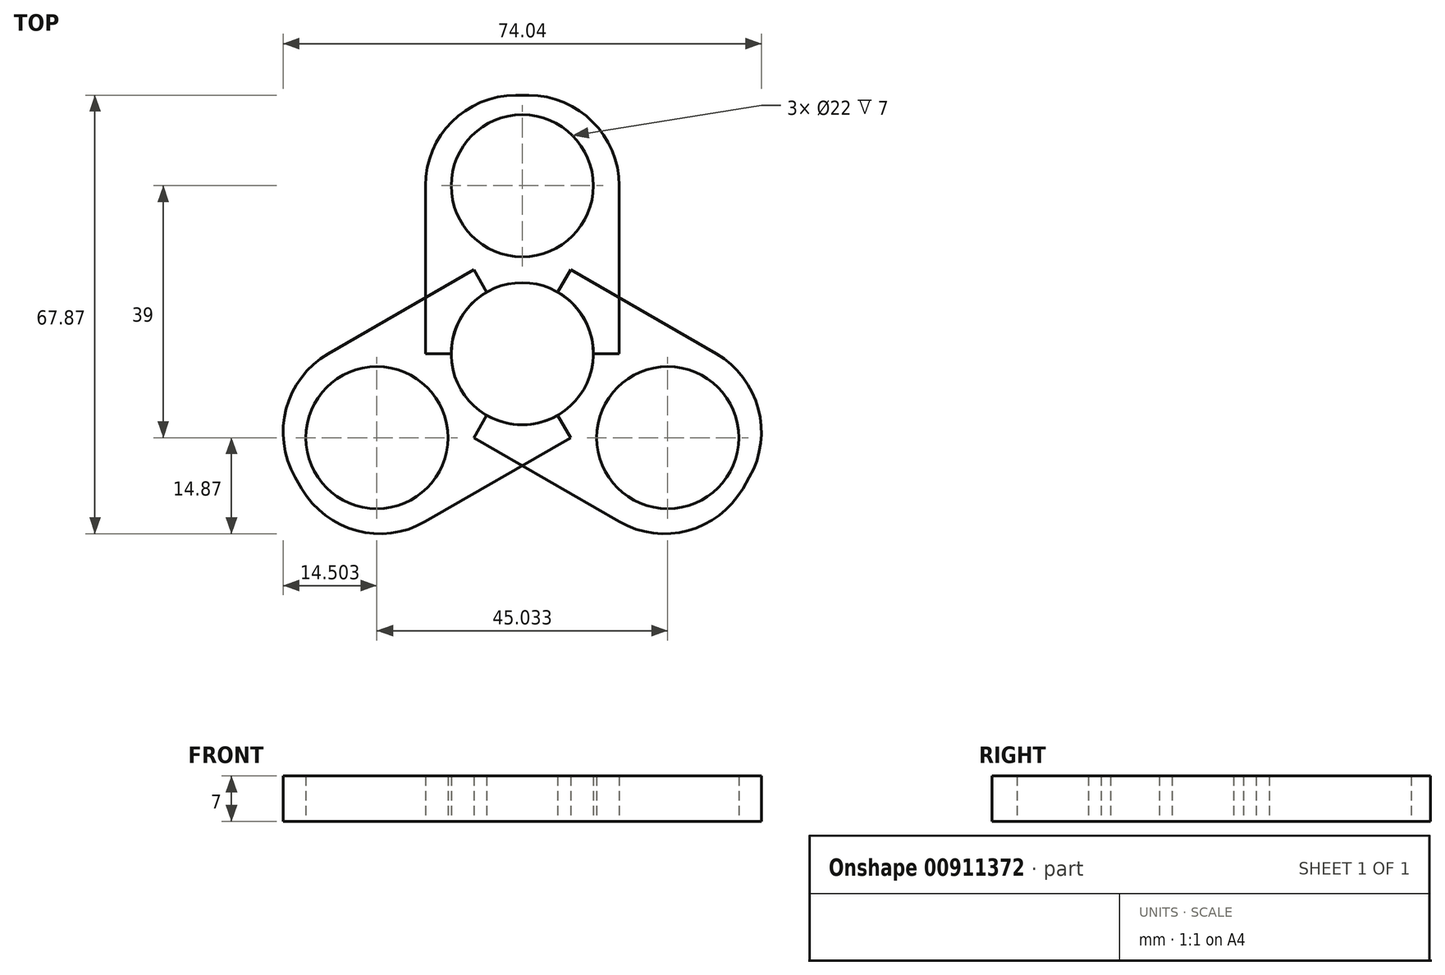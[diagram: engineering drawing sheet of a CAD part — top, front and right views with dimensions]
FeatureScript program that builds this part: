
annotation { "Feature Type Name" : "Feature", "Feature Type Description" : "" }
export const myFeature = defineFeature(function(context is Context, id is Id, definition is map)
    precondition{}
    {
        {
            var Q0;
            Q0=qCreatedBy(makeId("Top.planeOp"),FACE);
            var sketch = newSketch(context, id + "F0", { "sketchPlane" : qUnion([Q0])});
            skCircle(sketch, "E0", {"center": v(0, 0) * mm, "radius": 11 * mm});
            skLineSegment(sketch, "E1.bottom", {"start": v(0, 0) * mm, "end": v(15, 0) * mm});
            skLineSegment(sketch, "E1.top", {"start": v(0, 40) * mm, "end": v(1, 40) * mm});
            skLineSegment(sketch, "E1.left", {"start": v(0, 0) * mm, "end": v(0, 40) * mm});
            skLineSegment(sketch, "E1.right", {"start": v(15, 0) * mm, "end": v(15, 26) * mm});
            skLineSegment(sketch, "E2.bottom", {"start": v(0, 0) * mm, "end": v(-15, 0) * mm});
            skLineSegment(sketch, "E2.top", {"start": v(0, 40) * mm, "end": v(-1, 40) * mm});
            skLineSegment(sketch, "E2.right", {"start": v(-15, 0) * mm, "end": v(-15, 26) * mm});
            skLineSegment(sketch, "E3", {"start": v(0, 40) * mm, "end": v(0, 26) * mm});
            skCircle(sketch, "E4", {"center": v(0, 26) * mm, "radius": 11 * mm});
            skPoint(sketch, "E5.visualSharp", {"position": v(-15, 40) * mm});
            skArc(sketch, "E5.filletArc", {"start": v(-1, 40) * mm, "mid": v(-10.9, 35.9) * mm, "end": v(-15, 26) * mm});
            skPoint(sketch, "E6.visualSharp", {"position": v(15, 40) * mm});
            skArc(sketch, "E6.filletArc", {"start": v(15, 26) * mm, "mid": v(10.9, 35.9) * mm, "end": v(1, 40) * mm});
            skSolve(sketch);
        }
        {
            var Q0;
            {var subQ0=sQuery(id+"F0.wireOp",EDGE,"E2.top");Q0=makeQuery(id+"F0.imprint","IMPRINT",FACE,{"disambiguationData":[TD([[makeQuery(id+"F0.imprint","IMPRINT",EDGE,{"derivedFrom":subQ0}),1.0]])]});}
            var Q1;
            {var subQ9=sQuery(id+"F0.wireOp",EDGE,"E1.top");Q1=makeQuery(id+"F0.imprint","IMPRINT",FACE,{"disambiguationData":[TD([[makeQuery(id+"F0.imprint","IMPRINT",EDGE,{"derivedFrom":subQ9}),-1.0]])]});}
            extrude(context, id + "F1", {"entities" : qUnion([Q0, Q1]), "depth" : 7 * mm, "offsetDistance" : 25 * mm});
        }
        {
            var Q0;
            Q0=qCreatedBy(makeId("Front.planeOp"),FACE);
            var sketch = newSketch(context, id + "F2", { "sketchPlane" : qUnion([Q0])});
            skLineSegment(sketch, "E7", {"start": v(0, 0) * mm, "end": v(0, 51.16) * mm});
            skSolve(sketch);
        }
        {
            var Q0;
            Q0=makeQuery(id+"F1.opExtrude","SWEPT_BODY",BODY,{"disambiguationData":[OSD([sQuery(id+"F0.wireOp",EDGE,"E0"),sQuery(id+"F0.wireOp",EDGE,"E1.bottom"),sQuery(id+"F0.wireOp",EDGE,"E1.top"),sQuery(id+"F0.wireOp",EDGE,"E1.right"),sQuery(id+"F0.wireOp",EDGE,"E2.bottom"),sQuery(id+"F0.wireOp",EDGE,"E2.top"),sQuery(id+"F0.wireOp",EDGE,"E2.right"),sQuery(id+"F0.wireOp",EDGE,"E4")])]});
            var Q1;
            Q1=sQuery(id+"F2.wireOp",EDGE,"E7");
            transform(context, id + "F3", {"entities" : qUnion([Q0]), "transformType" : TransformType.ROTATION, "transformAxis" : qUnion([Q1]), "angle" : 120 * degree, "makeCopy" : true});
        }
        {
            var Q0;
            Q0=makeQuery(id+"F1.opExtrude","SWEPT_BODY",BODY,{"disambiguationData":[OSD([sQuery(id+"F0.wireOp",EDGE,"E0"),sQuery(id+"F0.wireOp",EDGE,"E1.bottom"),sQuery(id+"F0.wireOp",EDGE,"E1.top"),sQuery(id+"F0.wireOp",EDGE,"E1.right"),sQuery(id+"F0.wireOp",EDGE,"E2.bottom"),sQuery(id+"F0.wireOp",EDGE,"E2.top"),sQuery(id+"F0.wireOp",EDGE,"E2.right"),sQuery(id+"F0.wireOp",EDGE,"E4")])]});
            var Q1;
            Q1=sQuery(id+"F2.wireOp",EDGE,"E7");
            transform(context, id + "F4", {"entities" : qUnion([Q0]), "transformType" : TransformType.ROTATION, "transformAxis" : qUnion([Q1]), "angle" : 240 * degree, "makeCopy" : true});
        }
    });
